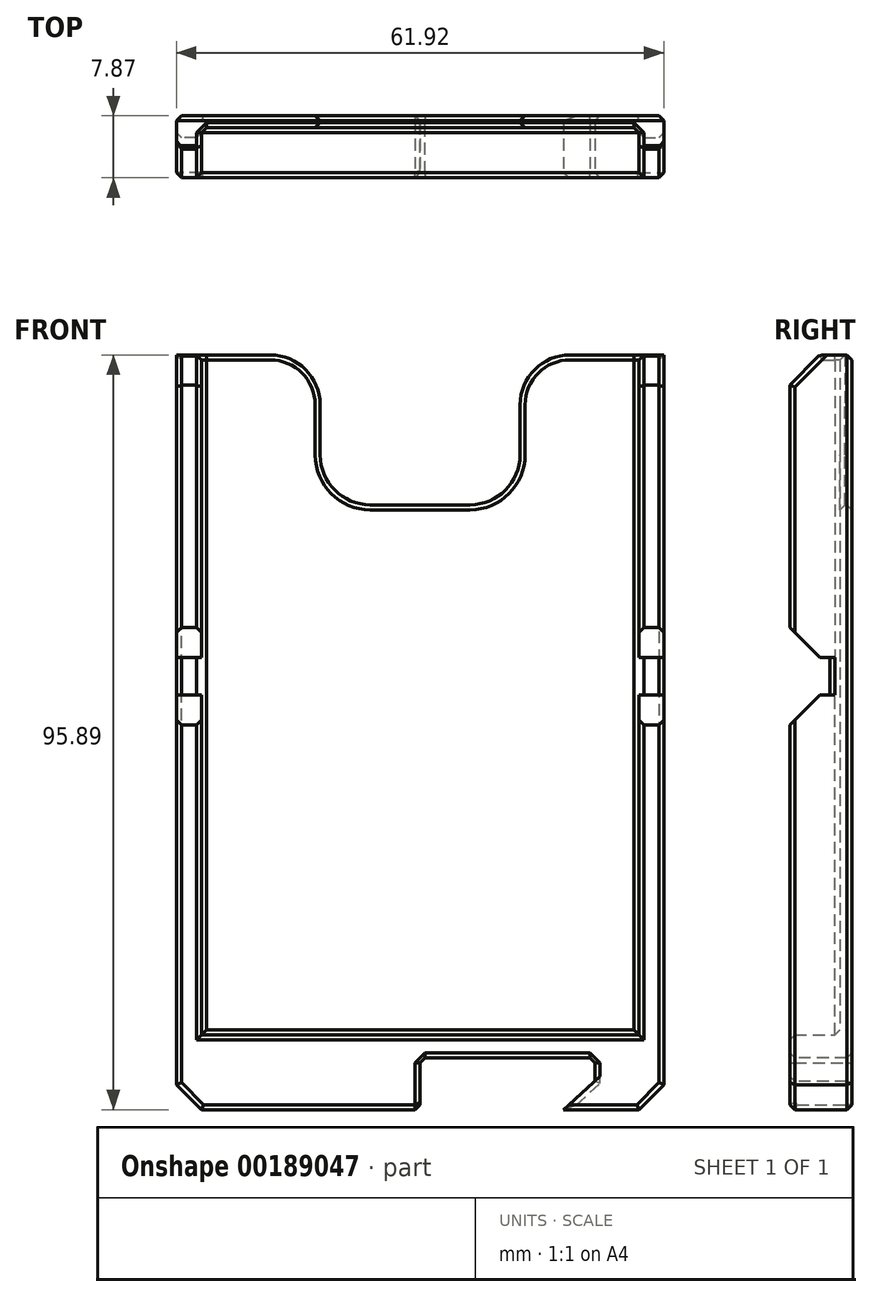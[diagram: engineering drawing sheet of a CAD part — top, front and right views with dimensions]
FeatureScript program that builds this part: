
annotation { "Feature Type Name" : "Feature", "Feature Type Description" : "" }
export const myFeature = defineFeature(function(context is Context, id is Id, definition is map)
    precondition{}
    {
        {
            var Q0;
            Q0=qCreatedBy(makeId("Front.planeOp"),FACE);
            var sketch = newSketch(context, id + "F0", { "sketchPlane" : qUnion([Q0])});
            skLineSegment(sketch, "E0.bottom", {"start": v(-19.05, 43.18) * mm, "end": v(-30.96, 43.18) * mm});
            skLineSegment(sketch, "E0.top", {"start": v(27.78, -43.18) * mm, "end": v(-27.78, -43.18) * mm});
            skLineSegment(sketch, "E0.left", {"start": v(27.78, 43.18) * mm, "end": v(27.78, -43.18) * mm});
            skLineSegment(sketch, "E0.right", {"start": v(-27.78, 43.18) * mm, "end": v(-27.78, -43.18) * mm});
            skPoint(sketch, "E0.middle", {"position": v(0, 0) * mm});
            skLineSegment(sketch, "E1.2", {"start": v(30.96, 43.18) * mm, "end": v(30.96, -52.7) * mm});
            skLineSegment(sketch, "E2.0", {"start": v(-30.96, 43.18) * mm, "end": v(-30.96, -52.7) * mm});
            skLineSegment(sketch, "E3.0", {"start": v(30.96, -52.7) * mm, "end": v(-30.96, -52.7) * mm});
            skLineSegment(sketch, "E4", {"start": v(27.78, 0) * mm, "end": v(30.96, 0) * mm});
            skLineSegment(sketch, "E5", {"start": v(-27.78, 0) * mm, "end": v(-30.96, 0) * mm});
            skLineSegment(sketch, "E6.0", {"start": v(-27.78, 4.76) * mm, "end": v(-30.96, 4.76) * mm});
            skLineSegment(sketch, "E7.0", {"start": v(27.78, 4.76) * mm, "end": v(30.96, 4.76) * mm});
            skLineSegment(sketch, "E8.bottom", {"start": v(6.35, 24.13) * mm, "end": v(-6.35, 24.13) * mm});
            skLineSegment(sketch, "E8.top", {"start": v(12.7, 62.23) * mm, "end": v(-12.7, 62.23) * mm});
            skLineSegment(sketch, "E8.left", {"start": v(12.7, 30.48) * mm, "end": v(12.7, 36.83) * mm});
            skLineSegment(sketch, "E8.right", {"start": v(-12.7, 30.48) * mm, "end": v(-12.7, 36.83) * mm});
            skPoint(sketch, "E8.middle", {"position": v(0, 43.18) * mm});
            skPoint(sketch, "E9.visualSharp", {"position": v(-12.7, 24.13) * mm});
            skArc(sketch, "E9.filletArc", {"start": v(-12.7, 30.48) * mm, "mid": v(-10.84, 25.99) * mm, "end": v(-6.35, 24.13) * mm});
            skPoint(sketch, "E10.visualSharp", {"position": v(12.7, 24.13) * mm});
            skArc(sketch, "E10.filletArc", {"start": v(6.35, 24.13) * mm, "mid": v(10.84, 25.99) * mm, "end": v(12.7, 30.48) * mm});
            skPoint(sketch, "E11.newPointA", {"position": v(-12.7, 62.23) * mm});
            skPoint(sketch, "E11.newPointB", {"position": v(30.96, 43.18) * mm});
            skArc(sketch, "E11.filletArc", {"start": v(-12.7, 36.83) * mm, "mid": v(-14.56, 41.32) * mm, "end": v(-19.05, 43.18) * mm});
            skLineSegment(sketch, "E12", {"start": v(27.78, 43.18) * mm, "end": v(19.05, 43.18) * mm});
            skArc(sketch, "E13.filletArc", {"start": v(19.05, 43.18) * mm, "mid": v(14.56, 41.32) * mm, "end": v(12.7, 36.83) * mm});
            skLineSegment(sketch, "E14", {"start": v(30.96, 43.18) * mm, "end": v(27.78, 43.18) * mm});
            skSolve(sketch);
        }
        {
            var Q0;
            {var subQ5=sQuery(id+"F0.wireOp",EDGE,"E0.top");Q0=makeQuery(id+"F0.imprint","IMPRINT",FACE,{"disambiguationData":[TD([[makeQuery(id+"F0.imprint","IMPRINT",EDGE,{"derivedFrom":subQ5}),-1.0]])]});}
            var Q1;
            {var subQ5=sQuery(id+"F0.wireOp",EDGE,"E6.0");Q1=makeQuery(id+"F0.imprint","IMPRINT",FACE,{"disambiguationData":[TD([[makeQuery(id+"F0.imprint","IMPRINT",EDGE,{"derivedFrom":subQ5}),-1.0]])]});}
            var Q2;
            {var subQ0=sQuery(id+"F0.wireOp",EDGE,"E5");Q2=makeQuery(id+"F0.imprint","IMPRINT",FACE,{"disambiguationData":[TD([[makeQuery(id+"F0.imprint","IMPRINT",EDGE,{"derivedFrom":subQ0}),-1.0]])]});}
            var Q3;
            {var subQ0=sQuery(id+"F0.wireOp",EDGE,"E4");Q3=makeQuery(id+"F0.imprint","IMPRINT",FACE,{"disambiguationData":[TD([[makeQuery(id+"F0.imprint","IMPRINT",EDGE,{"derivedFrom":subQ0}),1.0]])]});}
            var Q4;
            {var subQ5=sQuery(id+"F0.wireOp",EDGE,"E7.0");Q4=makeQuery(id+"F0.imprint","IMPRINT",FACE,{"disambiguationData":[TD([[makeQuery(id+"F0.imprint","IMPRINT",EDGE,{"derivedFrom":subQ5}),1.0]])]});}
            var Q5;
            {var subQ4=sQuery(id+"F0.wireOp",EDGE,"E0.top");Q5=makeQuery(id+"F0.imprint","IMPRINT",FACE,{"disambiguationData":[TD([[makeQuery(id+"F0.imprint","IMPRINT",EDGE,{"derivedFrom":subQ4}),1.0]])]});}
            extrude(context, id + "F1", {"entities" : qUnion([Q0, Q1, Q2, Q3, Q4, Q5]), "oppositeDirection" : true, "depth" : 1.52 * mm});
        }
        {
            var Q0;
            {var subQ4=sQuery(id+"F0.wireOp",EDGE,"E0.top");Q0=makeQuery(id+"F0.imprint","IMPRINT",FACE,{"disambiguationData":[TD([[makeQuery(id+"F0.imprint","IMPRINT",EDGE,{"derivedFrom":subQ4}),1.0]])]});}
            var Q1;
            {var subQ5=sQuery(id+"F0.wireOp",EDGE,"E7.0");Q1=makeQuery(id+"F0.imprint","IMPRINT",FACE,{"disambiguationData":[TD([[makeQuery(id+"F0.imprint","IMPRINT",EDGE,{"derivedFrom":subQ5}),1.0]])]});}
            var Q2;
            {var subQ5=sQuery(id+"F0.wireOp",EDGE,"E6.0");Q2=makeQuery(id+"F0.imprint","IMPRINT",FACE,{"disambiguationData":[TD([[makeQuery(id+"F0.imprint","IMPRINT",EDGE,{"derivedFrom":subQ5}),-1.0]])]});}
            extrude(context, id + "F2", {"entities" : qUnion([Q0, Q1, Q2]), "depth" : 6.35 * mm});
        }
        {
            var Q0;
            {var subQ0=sQuery(id+"F0.wireOp",EDGE,"E5");Q0=makeQuery(id+"F0.imprint","IMPRINT",FACE,{"disambiguationData":[TD([[makeQuery(id+"F0.imprint","IMPRINT",EDGE,{"derivedFrom":subQ0}),-1.0]])]});}
            var Q1;
            {var subQ0=sQuery(id+"F0.wireOp",EDGE,"E4");Q1=makeQuery(id+"F0.imprint","IMPRINT",FACE,{"disambiguationData":[TD([[makeQuery(id+"F0.imprint","IMPRINT",EDGE,{"derivedFrom":subQ0}),1.0]])]});}
            extrude(context, id + "F3", {"entities" : qUnion([Q0, Q1]), "depth" : 1.27 * mm});
        }
        {
            var Q0;
            Q0=makeQuery(id+"F2.opExtrude","SWEPT_BODY",BODY,{"disambiguationData":[OSD([sQuery(id+"F0.wireOp",EDGE,"E0.bottom"),sQuery(id+"F0.wireOp",EDGE,"E0.right"),sQuery(id+"F0.wireOp",EDGE,"E2.0"),sQuery(id+"F0.wireOp",EDGE,"E6.0")])]});
            var Q1;
            Q1=makeQuery(id+"F3.opExtrude","SWEPT_BODY",BODY,{"disambiguationData":[OSD([sQuery(id+"F0.wireOp",EDGE,"E0.right"),sQuery(id+"F0.wireOp",EDGE,"E2.0"),sQuery(id+"F0.wireOp",EDGE,"E5"),sQuery(id+"F0.wireOp",EDGE,"E6.0")])]});
            var Q2;
            Q2=makeQuery(id+"F2.opExtrude","SWEPT_BODY",BODY,{"disambiguationData":[OSD([sQuery(id+"F0.wireOp",EDGE,"E0.top"),sQuery(id+"F0.wireOp",EDGE,"E0.left"),sQuery(id+"F0.wireOp",EDGE,"E0.right"),sQuery(id+"F0.wireOp",EDGE,"E1.2"),sQuery(id+"F0.wireOp",EDGE,"E2.0"),sQuery(id+"F0.wireOp",EDGE,"E3.0"),sQuery(id+"F0.wireOp",EDGE,"E4"),sQuery(id+"F0.wireOp",EDGE,"E5")])]});
            var Q3;
            Q3=makeQuery(id+"F3.opExtrude","SWEPT_BODY",BODY,{"disambiguationData":[OSD([sQuery(id+"F0.wireOp",EDGE,"E0.left"),sQuery(id+"F0.wireOp",EDGE,"E1.2"),sQuery(id+"F0.wireOp",EDGE,"E4"),sQuery(id+"F0.wireOp",EDGE,"E7.0")])]});
            var Q4;
            Q4=makeQuery(id+"F2.opExtrude","SWEPT_BODY",BODY,{"disambiguationData":[OSD([sQuery(id+"F0.wireOp",EDGE,"E0.bottom"),sQuery(id+"F0.wireOp",EDGE,"E0.left"),sQuery(id+"F0.wireOp",EDGE,"E1.2"),sQuery(id+"F0.wireOp",EDGE,"E7.0")])]});
            booleanBodies(context, id + "F4", {"operationType" : BooleanOperationType.UNION, "tools" : qUnion([Q0, Q1, Q2, Q3, Q4])});
        }
        {
            var Q0;
            Q0=makeQuery(id+"F2.opExtrude","CAP_EDGE",EDGE,{"disambiguationData":[OSD([sQuery(id+"F0.wireOp",EDGE,"E6.0")])],"isStart":false});
            var Q1;
            Q1=makeQuery(id+"F2.opExtrude","CAP_EDGE",EDGE,{"disambiguationData":[OSD([sQuery(id+"F0.wireOp",EDGE,"E5")])],"isStart":false});
            var Q2;
            Q2=makeQuery(id+"F2.opExtrude","CAP_EDGE",EDGE,{"disambiguationData":[OSD([sQuery(id+"F0.wireOp",EDGE,"E7.0")])],"isStart":false});
            var Q3;
            Q3=makeQuery(id+"F2.opExtrude","CAP_EDGE",EDGE,{"disambiguationData":[OSD([sQuery(id+"F0.wireOp",EDGE,"E4")])],"isStart":false});
            var Q4;
            {var subQ0=sQuery(id+"F0.wireOp",EDGE,"E0.bottom");Q4=makeQuery(id+"F2.opExtrude","CAP_EDGE",EDGE,{"disambiguationData":[OSD([subQ0]),TDD([makeQuery(id+"F0.imprint","IMPRINT",EDGE,{"disambiguationData":[TD([[makeQuery(id+"F0.imprint","INTERSECT",VERTEX,{"derivedFrom":[subQ0,sQuery(id+"F0.wireOp",EDGE,"E2.0")]}),1.0]])],"derivedFrom":subQ0})])],"isStart":false});}
            var Q5;
            {var subQ0=sQuery(id+"F0.wireOp",EDGE,"E0.bottom");Q5=makeQuery(id+"F2.opExtrude","CAP_EDGE",EDGE,{"disambiguationData":[OSD([subQ0]),TDD([makeQuery(id+"F0.imprint","IMPRINT",EDGE,{"disambiguationData":[TD([[makeQuery(id+"F0.imprint","INTERSECT",VERTEX,{"derivedFrom":[subQ0,sQuery(id+"F0.wireOp",EDGE,"E1.2")]}),-1.0]])],"derivedFrom":subQ0})])],"isStart":false});}
            var Q6;
            Q6=makeQuery(id+"F2.opExtrude","CAP_EDGE",EDGE,{"disambiguationData":[OSD([sQuery(id+"F0.wireOp",EDGE,"E14")])],"isStart":false});
            chamfer(context, id + "F5", {"entities" : qUnion([Q0, Q1, Q2, Q3, Q4, Q5, Q6]), "width" : 3.8 * mm, "tangentPropagation" : true});
        }
        {
            var Q0;
            {var subQ0=sQuery(id+"F0.wireOp",EDGE,"E0.left");Q0=makeQuery(id+"F2.opExtrude","CAP_EDGE",EDGE,{"disambiguationData":[OSD([subQ0]),TDD([makeQuery(id+"F0.imprint","IMPRINT",EDGE,{"disambiguationData":[TD([[makeQuery(id+"F0.imprint","INTERSECT",VERTEX,{"derivedFrom":[sQuery(id+"F0.wireOp",EDGE,"E0.top"),subQ0]}),1.0]])],"derivedFrom":subQ0})])],"isStart":false});}
            var Q1;
            Q1=makeQuery(id+"F2.opExtrude","CAP_EDGE",EDGE,{"disambiguationData":[OSD([sQuery(id+"F0.wireOp",EDGE,"E0.top")])],"isStart":false});
            var Q2;
            {var subQ0=sQuery(id+"F0.wireOp",EDGE,"E0.right");Q2=makeQuery(id+"F2.opExtrude","CAP_EDGE",EDGE,{"disambiguationData":[OSD([subQ0]),TDD([makeQuery(id+"F0.imprint","IMPRINT",EDGE,{"disambiguationData":[TD([[makeQuery(id+"F0.imprint","INTERSECT",VERTEX,{"derivedFrom":[sQuery(id+"F0.wireOp",EDGE,"E0.top"),subQ0]}),1.0]])],"derivedFrom":subQ0})])],"isStart":false});}
            var Q3;
            {var subQ0=sQuery(id+"F0.wireOp",EDGE,"E0.right");Q3=makeQuery(id+"F2.opExtrude","CAP_EDGE",EDGE,{"disambiguationData":[OSD([subQ0]),TDD([makeQuery(id+"F0.imprint","IMPRINT",EDGE,{"disambiguationData":[TD([[makeQuery(id+"F0.imprint","INTERSECT",VERTEX,{"derivedFrom":[sQuery(id+"F0.wireOp",EDGE,"E0.bottom"),subQ0]}),-1.0]])],"derivedFrom":subQ0})])],"isStart":false});}
            var Q4;
            Q4=makeQuery(id+"F3.opExtrude","CAP_EDGE",EDGE,{"disambiguationData":[OSD([sQuery(id+"F0.wireOp",EDGE,"E2.0")])],"isStart":false});
            var Q5;
            Q5=makeQuery(id+"F3.opExtrude","CAP_EDGE",EDGE,{"disambiguationData":[OSD([sQuery(id+"F0.wireOp",EDGE,"E0.right")])],"isStart":false});
            var Q6;
            Q6=makeQuery(id+"F3.opExtrude","CAP_EDGE",EDGE,{"disambiguationData":[OSD([sQuery(id+"F0.wireOp",EDGE,"E0.left")])],"isStart":false});
            var Q7;
            Q7=makeQuery(id+"F3.opExtrude","CAP_EDGE",EDGE,{"disambiguationData":[OSD([sQuery(id+"F0.wireOp",EDGE,"E1.2")])],"isStart":false});
            var Q8;
            {var subQ0=sQuery(id+"F0.wireOp",EDGE,"E1.2");Q8=makeQuery(id+"F2.opExtrude","CAP_EDGE",EDGE,{"disambiguationData":[OSD([subQ0]),TDD([makeQuery(id+"F0.imprint","IMPRINT",EDGE,{"disambiguationData":[TD([[makeQuery(id+"F0.imprint","INTERSECT",VERTEX,{"derivedFrom":[subQ0,sQuery(id+"F0.wireOp",EDGE,"E14")]}),-1.0]])],"derivedFrom":subQ0})])],"isStart":false});}
            var Q9;
            {var subQ0=sQuery(id+"F0.wireOp",EDGE,"E1.2");Q9=makeQuery(id+"F2.opExtrude","CAP_EDGE",EDGE,{"disambiguationData":[OSD([subQ0]),TDD([makeQuery(id+"F0.imprint","IMPRINT",EDGE,{"disambiguationData":[TD([[makeQuery(id+"F0.imprint","INTERSECT",VERTEX,{"derivedFrom":[subQ0,sQuery(id+"F0.wireOp",EDGE,"E3.0")]}),1.0]])],"derivedFrom":subQ0})])],"isStart":false});}
            var Q10;
            {var subQ0=sQuery(id+"F0.wireOp",EDGE,"E2.0");Q10=makeQuery(id+"F2.opExtrude","CAP_EDGE",EDGE,{"disambiguationData":[OSD([subQ0]),TDD([makeQuery(id+"F0.imprint","IMPRINT",EDGE,{"disambiguationData":[TD([[makeQuery(id+"F0.imprint","INTERSECT",VERTEX,{"derivedFrom":[subQ0,sQuery(id+"F0.wireOp",EDGE,"E3.0")]}),1.0]])],"derivedFrom":subQ0})])],"isStart":false});}
            var Q11;
            {var subQ0=sQuery(id+"F0.wireOp",EDGE,"E2.0");Q11=makeQuery(id+"F2.opExtrude","CAP_EDGE",EDGE,{"disambiguationData":[OSD([subQ0]),TDD([makeQuery(id+"F0.imprint","IMPRINT",EDGE,{"disambiguationData":[TD([[makeQuery(id+"F0.imprint","INTERSECT",VERTEX,{"derivedFrom":[sQuery(id+"F0.wireOp",EDGE,"E0.bottom"),subQ0]}),-1.0]])],"derivedFrom":subQ0})])],"isStart":false});}
            var Q12;
            {var subQ0=sQuery(id+"F0.wireOp",EDGE,"E0.left");Q12=makeQuery(id+"F2.opExtrude","CAP_EDGE",EDGE,{"disambiguationData":[OSD([subQ0]),TDD([makeQuery(id+"F0.imprint","IMPRINT",EDGE,{"disambiguationData":[TD([[makeQuery(id+"F0.imprint","INTERSECT",VERTEX,{"derivedFrom":[subQ0,sQuery(id+"F0.wireOp",EDGE,"E7.0")]}),1.0]])],"derivedFrom":subQ0})])],"isStart":false});}
            var Q13;
            {var subQ0=sQuery(id+"F0.wireOp",EDGE,"E0.left");var subQ1=sQuery(id+"F0.wireOp",EDGE,"E14");Q13=makeQuery(id+"F5.opChamfer","BLEND_EDGE",EDGE,{"blendedFrom":[makeQuery(id+"F2.opExtrude","CAP_EDGE",EDGE,{"disambiguationData":[OSD([subQ1])],"isStart":false}),makeQuery(id+"F4.opBoolean","MERGE",FACE,{"derivedFrom":[makeQuery(id+"F2.opExtrude","SWEPT_FACE",FACE,{"disambiguationData":[OSD([subQ0]),TDD([makeQuery(id+"F0.imprint","IMPRINT",EDGE,{"disambiguationData":[TD([[makeQuery(id+"F0.imprint","INTERSECT",VERTEX,{"derivedFrom":[subQ0,sQuery(id+"F0.wireOp",EDGE,"E7.0")]}),1.0]])],"derivedFrom":subQ0})])]}),makeQuery(id+"F2.opExtrude","SWEPT_FACE",FACE,{"disambiguationData":[OSD([subQ0]),TDD([makeQuery(id+"F0.imprint","IMPRINT",EDGE,{"disambiguationData":[TD([[makeQuery(id+"F0.imprint","INTERSECT",VERTEX,{"derivedFrom":[sQuery(id+"F0.wireOp",EDGE,"E0.top"),subQ0]}),1.0]])],"derivedFrom":subQ0})])]}),makeQuery(id+"F3.opExtrude","SWEPT_FACE",FACE,{"disambiguationData":[OSD([subQ0])]})]})],"blendedInto":[makeQuery(id+"F4.opBoolean","MERGE",FACE,{"derivedFrom":[makeQuery(id+"F2.opExtrude","SWEPT_FACE",FACE,{"disambiguationData":[OSD([subQ0]),TDD([makeQuery(id+"F0.imprint","IMPRINT",EDGE,{"disambiguationData":[TD([[makeQuery(id+"F0.imprint","INTERSECT",VERTEX,{"derivedFrom":[subQ0,sQuery(id+"F0.wireOp",EDGE,"E7.0")]}),1.0]])],"derivedFrom":subQ0})])]}),makeQuery(id+"F2.opExtrude","SWEPT_FACE",FACE,{"disambiguationData":[OSD([subQ0]),TDD([makeQuery(id+"F0.imprint","IMPRINT",EDGE,{"disambiguationData":[TD([[makeQuery(id+"F0.imprint","INTERSECT",VERTEX,{"derivedFrom":[sQuery(id+"F0.wireOp",EDGE,"E0.top"),subQ0]}),1.0]])],"derivedFrom":subQ0})])]}),makeQuery(id+"F3.opExtrude","SWEPT_FACE",FACE,{"disambiguationData":[OSD([subQ0])]})]})]});}
            var Q14;
            {var subQ0=sQuery(id+"F0.wireOp",EDGE,"E1.2");var subQ1=sQuery(id+"F0.wireOp",EDGE,"E14");Q14=makeQuery(id+"F5.opChamfer","BLEND_EDGE",EDGE,{"blendedFrom":[makeQuery(id+"F2.opExtrude","CAP_EDGE",EDGE,{"disambiguationData":[OSD([subQ1])],"isStart":false}),makeQuery(id+"F4.opBoolean","MERGE",FACE,{"derivedFrom":[makeQuery(id+"F2.opExtrude","SWEPT_FACE",FACE,{"disambiguationData":[OSD([subQ0]),TDD([makeQuery(id+"F0.imprint","IMPRINT",EDGE,{"disambiguationData":[TD([[makeQuery(id+"F0.imprint","INTERSECT",VERTEX,{"derivedFrom":[subQ0,subQ1]}),-1.0]])],"derivedFrom":subQ0})])]}),makeQuery(id+"F2.opExtrude","SWEPT_FACE",FACE,{"disambiguationData":[OSD([subQ0]),TDD([makeQuery(id+"F0.imprint","IMPRINT",EDGE,{"disambiguationData":[TD([[makeQuery(id+"F0.imprint","INTERSECT",VERTEX,{"derivedFrom":[subQ0,sQuery(id+"F0.wireOp",EDGE,"E3.0")]}),1.0]])],"derivedFrom":subQ0})])]}),makeQuery(id+"F3.opExtrude","SWEPT_FACE",FACE,{"disambiguationData":[OSD([subQ0])]})]})],"blendedInto":[makeQuery(id+"F4.opBoolean","MERGE",FACE,{"derivedFrom":[makeQuery(id+"F2.opExtrude","SWEPT_FACE",FACE,{"disambiguationData":[OSD([subQ0]),TDD([makeQuery(id+"F0.imprint","IMPRINT",EDGE,{"disambiguationData":[TD([[makeQuery(id+"F0.imprint","INTERSECT",VERTEX,{"derivedFrom":[subQ0,subQ1]}),-1.0]])],"derivedFrom":subQ0})])]}),makeQuery(id+"F2.opExtrude","SWEPT_FACE",FACE,{"disambiguationData":[OSD([subQ0]),TDD([makeQuery(id+"F0.imprint","IMPRINT",EDGE,{"disambiguationData":[TD([[makeQuery(id+"F0.imprint","INTERSECT",VERTEX,{"derivedFrom":[subQ0,sQuery(id+"F0.wireOp",EDGE,"E3.0")]}),1.0]])],"derivedFrom":subQ0})])]}),makeQuery(id+"F3.opExtrude","SWEPT_FACE",FACE,{"disambiguationData":[OSD([subQ0])]})]})]});}
            var Q15;
            {var subQ0=sQuery(id+"F0.wireOp",EDGE,"E2.0");var subQ1=sQuery(id+"F0.wireOp",EDGE,"E0.bottom");Q15=makeQuery(id+"F5.opChamfer","BLEND_EDGE",EDGE,{"blendedFrom":[makeQuery(id+"F2.opExtrude","CAP_EDGE",EDGE,{"disambiguationData":[OSD([subQ1])],"isStart":false}),makeQuery(id+"F4.opBoolean","MERGE",FACE,{"derivedFrom":[makeQuery(id+"F2.opExtrude","SWEPT_FACE",FACE,{"disambiguationData":[OSD([subQ0]),TDD([makeQuery(id+"F0.imprint","IMPRINT",EDGE,{"disambiguationData":[TD([[makeQuery(id+"F0.imprint","INTERSECT",VERTEX,{"derivedFrom":[subQ1,subQ0]}),-1.0]])],"derivedFrom":subQ0})])]}),makeQuery(id+"F2.opExtrude","SWEPT_FACE",FACE,{"disambiguationData":[OSD([subQ0]),TDD([makeQuery(id+"F0.imprint","IMPRINT",EDGE,{"disambiguationData":[TD([[makeQuery(id+"F0.imprint","INTERSECT",VERTEX,{"derivedFrom":[subQ0,sQuery(id+"F0.wireOp",EDGE,"E3.0")]}),1.0]])],"derivedFrom":subQ0})])]}),makeQuery(id+"F3.opExtrude","SWEPT_FACE",FACE,{"disambiguationData":[OSD([subQ0])]})]})],"blendedInto":[makeQuery(id+"F4.opBoolean","MERGE",FACE,{"derivedFrom":[makeQuery(id+"F2.opExtrude","SWEPT_FACE",FACE,{"disambiguationData":[OSD([subQ0]),TDD([makeQuery(id+"F0.imprint","IMPRINT",EDGE,{"disambiguationData":[TD([[makeQuery(id+"F0.imprint","INTERSECT",VERTEX,{"derivedFrom":[subQ1,subQ0]}),-1.0]])],"derivedFrom":subQ0})])]}),makeQuery(id+"F2.opExtrude","SWEPT_FACE",FACE,{"disambiguationData":[OSD([subQ0]),TDD([makeQuery(id+"F0.imprint","IMPRINT",EDGE,{"disambiguationData":[TD([[makeQuery(id+"F0.imprint","INTERSECT",VERTEX,{"derivedFrom":[subQ0,sQuery(id+"F0.wireOp",EDGE,"E3.0")]}),1.0]])],"derivedFrom":subQ0})])]}),makeQuery(id+"F3.opExtrude","SWEPT_FACE",FACE,{"disambiguationData":[OSD([subQ0])]})]})]});}
            var Q16;
            {var subQ0=sQuery(id+"F0.wireOp",EDGE,"E0.right");var subQ1=sQuery(id+"F0.wireOp",EDGE,"E0.bottom");Q16=makeQuery(id+"F5.opChamfer","BLEND_EDGE",EDGE,{"blendedFrom":[makeQuery(id+"F2.opExtrude","CAP_EDGE",EDGE,{"disambiguationData":[OSD([subQ1])],"isStart":false}),makeQuery(id+"F4.opBoolean","MERGE",FACE,{"derivedFrom":[makeQuery(id+"F2.opExtrude","SWEPT_FACE",FACE,{"disambiguationData":[OSD([subQ0]),TDD([makeQuery(id+"F0.imprint","IMPRINT",EDGE,{"disambiguationData":[TD([[makeQuery(id+"F0.imprint","INTERSECT",VERTEX,{"derivedFrom":[subQ1,subQ0]}),-1.0]])],"derivedFrom":subQ0})])]}),makeQuery(id+"F2.opExtrude","SWEPT_FACE",FACE,{"disambiguationData":[OSD([subQ0]),TDD([makeQuery(id+"F0.imprint","IMPRINT",EDGE,{"disambiguationData":[TD([[makeQuery(id+"F0.imprint","INTERSECT",VERTEX,{"derivedFrom":[sQuery(id+"F0.wireOp",EDGE,"E0.top"),subQ0]}),1.0]])],"derivedFrom":subQ0})])]}),makeQuery(id+"F3.opExtrude","SWEPT_FACE",FACE,{"disambiguationData":[OSD([subQ0])]})]})],"blendedInto":[makeQuery(id+"F4.opBoolean","MERGE",FACE,{"derivedFrom":[makeQuery(id+"F2.opExtrude","SWEPT_FACE",FACE,{"disambiguationData":[OSD([subQ0]),TDD([makeQuery(id+"F0.imprint","IMPRINT",EDGE,{"disambiguationData":[TD([[makeQuery(id+"F0.imprint","INTERSECT",VERTEX,{"derivedFrom":[subQ1,subQ0]}),-1.0]])],"derivedFrom":subQ0})])]}),makeQuery(id+"F2.opExtrude","SWEPT_FACE",FACE,{"disambiguationData":[OSD([subQ0]),TDD([makeQuery(id+"F0.imprint","IMPRINT",EDGE,{"disambiguationData":[TD([[makeQuery(id+"F0.imprint","INTERSECT",VERTEX,{"derivedFrom":[sQuery(id+"F0.wireOp",EDGE,"E0.top"),subQ0]}),1.0]])],"derivedFrom":subQ0})])]}),makeQuery(id+"F3.opExtrude","SWEPT_FACE",FACE,{"disambiguationData":[OSD([subQ0])]})]})]});}
            var Q17;
            {var subQ0=sQuery(id+"F0.wireOp",EDGE,"E0.bottom");Q17=makeQuery(id+"F5.opChamfer","BLEND_EDGE",EDGE,{"blendedFrom":[makeQuery(id+"F2.opExtrude","CAP_EDGE",EDGE,{"disambiguationData":[OSD([subQ0])],"isStart":false}),makeQuery(id+"F2.opExtrude","SWEPT_FACE",FACE,{"disambiguationData":[OSD([subQ0])]})],"blendedInto":[makeQuery(id+"F2.opExtrude","SWEPT_FACE",FACE,{"disambiguationData":[OSD([subQ0])]})]});}
            var Q18;
            {var subQ0=sQuery(id+"F0.wireOp",EDGE,"E14");Q18=makeQuery(id+"F5.opChamfer","BLEND_EDGE",EDGE,{"blendedFrom":[makeQuery(id+"F2.opExtrude","CAP_EDGE",EDGE,{"disambiguationData":[OSD([subQ0])],"isStart":false}),makeQuery(id+"F2.opExtrude","SWEPT_FACE",FACE,{"disambiguationData":[OSD([subQ0])]})],"blendedInto":[makeQuery(id+"F2.opExtrude","SWEPT_FACE",FACE,{"disambiguationData":[OSD([subQ0])]})]});}
            var Q19;
            Q19=makeQuery(id+"F2.opExtrude","CAP_EDGE",EDGE,{"disambiguationData":[OSD([sQuery(id+"F0.wireOp",EDGE,"E3.0")])],"isStart":false});
            chamfer(context, id + "F6", {"entities" : qUnion([Q0, Q1, Q2, Q3, Q4, Q5, Q6, Q7, Q8, Q9, Q10, Q11, Q12, Q13, Q14, Q15, Q16, Q17, Q18, Q19]), "width" : 0.64 * mm, "tangentPropagation" : true});
        }
        {
            var Q0;
            Q0=makeQuery(id+"F2.opExtrude","CAP_FACE",FACE,{"disambiguationData":[OSD([sQuery(id+"F0.wireOp",EDGE,"E0.top"),sQuery(id+"F0.wireOp",EDGE,"E0.left"),sQuery(id+"F0.wireOp",EDGE,"E0.right"),sQuery(id+"F0.wireOp",EDGE,"E1.2"),sQuery(id+"F0.wireOp",EDGE,"E2.0"),sQuery(id+"F0.wireOp",EDGE,"E3.0"),sQuery(id+"F0.wireOp",EDGE,"E4"),sQuery(id+"F0.wireOp",EDGE,"E5")])],"isStart":false});
            var sketch = newSketch(context, id + "F7", { "sketchPlane" : qUnion([Q0])});
            skLineSegment(sketch, "E15.bottom", {"start": v(0, -52.07) * mm, "end": v(22.23, -52.07) * mm});
            skLineSegment(sketch, "E15.top", {"start": v(0, -46.1) * mm, "end": v(22.23, -46.1) * mm});
            skLineSegment(sketch, "E15.left", {"start": v(0, -52.7) * mm, "end": v(0, -46.1) * mm});
            skLineSegment(sketch, "E15.right", {"start": v(22.23, -52.07) * mm, "end": v(22.23, -46.1) * mm});
            skLineSegment(sketch, "E16", {"start": v(22.23, -49.09) * mm, "end": v(18.22, -52.7) * mm});
            skLineSegment(sketch, "E17.0", {"start": v(30.96, -52.7) * mm, "end": v(-30.96, -52.7) * mm});
            skLineSegment(sketch, "E18", {"start": v(22.23, -52.07) * mm, "end": v(22.23, -52.7) * mm});
            skPoint(sketch, "E19.orphan", {"position": v(18.92, -52.07) * mm});
            skSolve(sketch);
        }
        {
            var Q0;
            Q0=makeQuery(id+"F1.opExtrude","SWEPT_BODY",BODY,{"disambiguationData":[OSD([sQuery(id+"F0.wireOp",EDGE,"E0.bottom"),sQuery(id+"F0.wireOp",EDGE,"E1.2"),sQuery(id+"F0.wireOp",EDGE,"E2.0"),sQuery(id+"F0.wireOp",EDGE,"E3.0"),sQuery(id+"F0.wireOp",EDGE,"E8.bottom"),sQuery(id+"F0.wireOp",EDGE,"E8.left"),sQuery(id+"F0.wireOp",EDGE,"E8.right"),sQuery(id+"F0.wireOp",EDGE,"E9.filletArc"),sQuery(id+"F0.wireOp",EDGE,"E10.filletArc"),sQuery(id+"F0.wireOp",EDGE,"E11.filletArc"),sQuery(id+"F0.wireOp",EDGE,"E12"),sQuery(id+"F0.wireOp",EDGE,"E13.filletArc"),sQuery(id+"F0.wireOp",EDGE,"E14")])]});
            var Q1;
            Q1=makeQuery(id+"F2.opExtrude","SWEPT_BODY",BODY,{"disambiguationData":[OSD([sQuery(id+"F0.wireOp",EDGE,"E0.bottom"),sQuery(id+"F0.wireOp",EDGE,"E0.right"),sQuery(id+"F0.wireOp",EDGE,"E2.0"),sQuery(id+"F0.wireOp",EDGE,"E6.0")])]});
            booleanBodies(context, id + "F8", {"operationType" : BooleanOperationType.UNION, "tools" : qUnion([Q0, Q1])});
        }
        {
            var Q0;
            {var subQ2=sQuery(id+"F7.wireOp",EDGE,"E15.top");Q0=makeQuery(id+"F7.imprint","IMPRINT",FACE,{"disambiguationData":[TD([[makeQuery(id+"F7.imprint","IMPRINT",EDGE,{"derivedFrom":subQ2}),-1.0]])]});}
            var Q1;
            {var subQ4=sQuery(id+"F7.wireOp",EDGE,"E16");var subQ6=sQuery(id+"F7.wireOp",EDGE,"E17.0");var subQ7=makeQuery(id+"F7.imprint","INTERSECT",VERTEX,{"derivedFrom":[subQ4,subQ6]});Q1=makeQuery(id+"F7.imprint","IMPRINT",FACE,{"disambiguationData":[TD([[makeQuery(id+"F7.imprint","IMPRINT",EDGE,{"disambiguationData":[TD([[subQ7,1.0]])],"derivedFrom":subQ4}),-1.0]])]});}
            extrude(context, id + "F9", {"entities" : qUnion([Q0, Q1]), "operationType" : NewBodyOperationType.REMOVE, "oppositeDirection" : true, "depth" : 25.4 * mm});
        }
        {
            var Q0;
            {var subQ0=sQuery(id+"F0.wireOp",EDGE,"E3.0");var subQ1=sQuery(id+"F0.wireOp",EDGE,"E1.2");Q0=makeQuery(id+"F8.opBoolean","MERGE",EDGE,{"derivedFrom":[makeQuery(id+"F1.opExtrude","SWEPT_EDGE",EDGE,{"disambiguationData":[OSD([subQ1,subQ0])]}),makeQuery(id+"F2.opExtrude","SWEPT_EDGE",EDGE,{"disambiguationData":[OSD([subQ1,subQ0])]})]});}
            var Q1;
            {var subQ0=sQuery(id+"F0.wireOp",EDGE,"E3.0");var subQ1=sQuery(id+"F0.wireOp",EDGE,"E2.0");Q1=makeQuery(id+"F8.opBoolean","MERGE",EDGE,{"derivedFrom":[makeQuery(id+"F1.opExtrude","SWEPT_EDGE",EDGE,{"disambiguationData":[OSD([subQ1,subQ0])]}),makeQuery(id+"F2.opExtrude","SWEPT_EDGE",EDGE,{"disambiguationData":[OSD([subQ1,subQ0])]})]});}
            chamfer(context, id + "F10", {"entities" : qUnion([Q0, Q1]), "width" : 3.17 * mm, "tangentPropagation" : true});
        }
        {
            var Q0;
            {var subQ0=sQuery(id+"F0.wireOp",EDGE,"E3.0");var subQ1=sQuery(id+"F0.wireOp",EDGE,"E1.2");Q0=makeQuery(id+"F10.opChamfer","BLEND_EDGE",EDGE,{"blendedFrom":[makeQuery(id+"F8.opBoolean","MERGE",EDGE,{"derivedFrom":[makeQuery(id+"F1.opExtrude","SWEPT_EDGE",EDGE,{"disambiguationData":[OSD([subQ1,subQ0])]}),makeQuery(id+"F2.opExtrude","SWEPT_EDGE",EDGE,{"disambiguationData":[OSD([subQ1,subQ0])]})]}),makeQuery(id+"F2.opExtrude","CAP_FACE",FACE,{"disambiguationData":[OSD([sQuery(id+"F0.wireOp",EDGE,"E0.top"),sQuery(id+"F0.wireOp",EDGE,"E0.left"),sQuery(id+"F0.wireOp",EDGE,"E0.right"),subQ1,sQuery(id+"F0.wireOp",EDGE,"E2.0"),subQ0,sQuery(id+"F0.wireOp",EDGE,"E4"),sQuery(id+"F0.wireOp",EDGE,"E5")])],"isStart":false})],"blendedInto":[makeQuery(id+"F2.opExtrude","CAP_FACE",FACE,{"disambiguationData":[OSD([sQuery(id+"F0.wireOp",EDGE,"E0.top"),sQuery(id+"F0.wireOp",EDGE,"E0.left"),sQuery(id+"F0.wireOp",EDGE,"E0.right"),subQ1,sQuery(id+"F0.wireOp",EDGE,"E2.0"),subQ0,sQuery(id+"F0.wireOp",EDGE,"E4"),sQuery(id+"F0.wireOp",EDGE,"E5")])],"isStart":false})]});}
            var Q1;
            {var subQ0=sQuery(id+"F0.wireOp",EDGE,"E3.0");var subQ1=sQuery(id+"F0.wireOp",EDGE,"E1.2");Q1=makeQuery(id+"F10.opChamfer","BLEND_EDGE",EDGE,{"blendedFrom":[makeQuery(id+"F8.opBoolean","MERGE",EDGE,{"derivedFrom":[makeQuery(id+"F1.opExtrude","SWEPT_EDGE",EDGE,{"disambiguationData":[OSD([subQ1,subQ0])]}),makeQuery(id+"F2.opExtrude","SWEPT_EDGE",EDGE,{"disambiguationData":[OSD([subQ1,subQ0])]})]}),makeQuery(id+"F1.opExtrude","CAP_FACE",FACE,{"disambiguationData":[OSD([sQuery(id+"F0.wireOp",EDGE,"E0.bottom"),subQ1,sQuery(id+"F0.wireOp",EDGE,"E2.0"),subQ0,sQuery(id+"F0.wireOp",EDGE,"E8.bottom"),sQuery(id+"F0.wireOp",EDGE,"E8.left"),sQuery(id+"F0.wireOp",EDGE,"E8.right"),sQuery(id+"F0.wireOp",EDGE,"E9.filletArc"),sQuery(id+"F0.wireOp",EDGE,"E10.filletArc"),sQuery(id+"F0.wireOp",EDGE,"E11.filletArc"),sQuery(id+"F0.wireOp",EDGE,"E12"),sQuery(id+"F0.wireOp",EDGE,"E13.filletArc"),sQuery(id+"F0.wireOp",EDGE,"E14")])],"isStart":false})],"blendedInto":[makeQuery(id+"F1.opExtrude","CAP_FACE",FACE,{"disambiguationData":[OSD([sQuery(id+"F0.wireOp",EDGE,"E0.bottom"),subQ1,sQuery(id+"F0.wireOp",EDGE,"E2.0"),subQ0,sQuery(id+"F0.wireOp",EDGE,"E8.bottom"),sQuery(id+"F0.wireOp",EDGE,"E8.left"),sQuery(id+"F0.wireOp",EDGE,"E8.right"),sQuery(id+"F0.wireOp",EDGE,"E9.filletArc"),sQuery(id+"F0.wireOp",EDGE,"E10.filletArc"),sQuery(id+"F0.wireOp",EDGE,"E11.filletArc"),sQuery(id+"F0.wireOp",EDGE,"E12"),sQuery(id+"F0.wireOp",EDGE,"E13.filletArc"),sQuery(id+"F0.wireOp",EDGE,"E14")])],"isStart":false})]});}
            var Q2;
            {var subQ0=sQuery(id+"F0.wireOp",EDGE,"E3.0");var subQ1=sQuery(id+"F0.wireOp",EDGE,"E2.0");Q2=makeQuery(id+"F10.opChamfer","BLEND_EDGE",EDGE,{"blendedFrom":[makeQuery(id+"F8.opBoolean","MERGE",EDGE,{"derivedFrom":[makeQuery(id+"F1.opExtrude","SWEPT_EDGE",EDGE,{"disambiguationData":[OSD([subQ1,subQ0])]}),makeQuery(id+"F2.opExtrude","SWEPT_EDGE",EDGE,{"disambiguationData":[OSD([subQ1,subQ0])]})]}),makeQuery(id+"F2.opExtrude","CAP_FACE",FACE,{"disambiguationData":[OSD([sQuery(id+"F0.wireOp",EDGE,"E0.top"),sQuery(id+"F0.wireOp",EDGE,"E0.left"),sQuery(id+"F0.wireOp",EDGE,"E0.right"),sQuery(id+"F0.wireOp",EDGE,"E1.2"),subQ1,subQ0,sQuery(id+"F0.wireOp",EDGE,"E4"),sQuery(id+"F0.wireOp",EDGE,"E5")])],"isStart":false})],"blendedInto":[makeQuery(id+"F2.opExtrude","CAP_FACE",FACE,{"disambiguationData":[OSD([sQuery(id+"F0.wireOp",EDGE,"E0.top"),sQuery(id+"F0.wireOp",EDGE,"E0.left"),sQuery(id+"F0.wireOp",EDGE,"E0.right"),sQuery(id+"F0.wireOp",EDGE,"E1.2"),subQ1,subQ0,sQuery(id+"F0.wireOp",EDGE,"E4"),sQuery(id+"F0.wireOp",EDGE,"E5")])],"isStart":false})]});}
            var Q3;
            {var subQ0=sQuery(id+"F0.wireOp",EDGE,"E3.0");var subQ1=sQuery(id+"F0.wireOp",EDGE,"E2.0");Q3=makeQuery(id+"F10.opChamfer","BLEND_EDGE",EDGE,{"blendedFrom":[makeQuery(id+"F8.opBoolean","MERGE",EDGE,{"derivedFrom":[makeQuery(id+"F1.opExtrude","SWEPT_EDGE",EDGE,{"disambiguationData":[OSD([subQ1,subQ0])]}),makeQuery(id+"F2.opExtrude","SWEPT_EDGE",EDGE,{"disambiguationData":[OSD([subQ1,subQ0])]})]}),makeQuery(id+"F1.opExtrude","CAP_FACE",FACE,{"disambiguationData":[OSD([sQuery(id+"F0.wireOp",EDGE,"E0.bottom"),sQuery(id+"F0.wireOp",EDGE,"E1.2"),subQ1,subQ0,sQuery(id+"F0.wireOp",EDGE,"E8.bottom"),sQuery(id+"F0.wireOp",EDGE,"E8.left"),sQuery(id+"F0.wireOp",EDGE,"E8.right"),sQuery(id+"F0.wireOp",EDGE,"E9.filletArc"),sQuery(id+"F0.wireOp",EDGE,"E10.filletArc"),sQuery(id+"F0.wireOp",EDGE,"E11.filletArc"),sQuery(id+"F0.wireOp",EDGE,"E12"),sQuery(id+"F0.wireOp",EDGE,"E13.filletArc"),sQuery(id+"F0.wireOp",EDGE,"E14")])],"isStart":false})],"blendedInto":[makeQuery(id+"F1.opExtrude","CAP_FACE",FACE,{"disambiguationData":[OSD([sQuery(id+"F0.wireOp",EDGE,"E0.bottom"),sQuery(id+"F0.wireOp",EDGE,"E1.2"),subQ1,subQ0,sQuery(id+"F0.wireOp",EDGE,"E8.bottom"),sQuery(id+"F0.wireOp",EDGE,"E8.left"),sQuery(id+"F0.wireOp",EDGE,"E8.right"),sQuery(id+"F0.wireOp",EDGE,"E9.filletArc"),sQuery(id+"F0.wireOp",EDGE,"E10.filletArc"),sQuery(id+"F0.wireOp",EDGE,"E11.filletArc"),sQuery(id+"F0.wireOp",EDGE,"E12"),sQuery(id+"F0.wireOp",EDGE,"E13.filletArc"),sQuery(id+"F0.wireOp",EDGE,"E14")])],"isStart":false})]});}
            var Q4;
            {var subQ1=sQuery(id+"F0.wireOp",EDGE,"E1.2");var subQ2=sQuery(id+"F0.wireOp",EDGE,"E3.0");Q4=makeQuery(id+"F9.boolean.opBoolean","SPLIT",EDGE,{"disambiguationData":[TD([makeQuery(id+"F1.opExtrude","SWEPT_FACE",FACE,{"disambiguationData":[OSD([subQ1])]})])],"derivedFrom":makeQuery(id+"F1.opExtrude","CAP_EDGE",EDGE,{"disambiguationData":[OSD([subQ2])],"isStart":false})});}
            var Q5;
            {var subQ0=sQuery(id+"F0.wireOp",EDGE,"E2.0");var subQ2=sQuery(id+"F0.wireOp",EDGE,"E3.0");Q5=makeQuery(id+"F9.boolean.opBoolean","SPLIT",EDGE,{"disambiguationData":[TD([makeQuery(id+"F1.opExtrude","SWEPT_FACE",FACE,{"disambiguationData":[OSD([subQ0])]})])],"derivedFrom":makeQuery(id+"F1.opExtrude","CAP_EDGE",EDGE,{"disambiguationData":[OSD([subQ2])],"isStart":false})});}
            var Q6;
            Q6=makeQuery(id+"F9.boolean.opBoolean","INTERSECT",EDGE,{"derivedFrom":[makeQuery(id+"F1.opExtrude","CAP_FACE",FACE,{"disambiguationData":[OSD([sQuery(id+"F0.wireOp",EDGE,"E0.bottom"),sQuery(id+"F0.wireOp",EDGE,"E1.2"),sQuery(id+"F0.wireOp",EDGE,"E2.0"),sQuery(id+"F0.wireOp",EDGE,"E3.0"),sQuery(id+"F0.wireOp",EDGE,"E8.bottom"),sQuery(id+"F0.wireOp",EDGE,"E8.left"),sQuery(id+"F0.wireOp",EDGE,"E8.right"),sQuery(id+"F0.wireOp",EDGE,"E9.filletArc"),sQuery(id+"F0.wireOp",EDGE,"E10.filletArc"),sQuery(id+"F0.wireOp",EDGE,"E11.filletArc"),sQuery(id+"F0.wireOp",EDGE,"E12"),sQuery(id+"F0.wireOp",EDGE,"E13.filletArc"),sQuery(id+"F0.wireOp",EDGE,"E14")])],"isStart":false}),makeQuery(id+"F9.opExtrude","SWEPT_FACE",FACE,{"disambiguationData":[OSD([sQuery(id+"F7.wireOp",EDGE,"E15.left")])]})]});
            var Q7;
            Q7=makeQuery(id+"F9.boolean.opBoolean","INTERSECT",EDGE,{"derivedFrom":[makeQuery(id+"F1.opExtrude","CAP_FACE",FACE,{"disambiguationData":[OSD([sQuery(id+"F0.wireOp",EDGE,"E0.bottom"),sQuery(id+"F0.wireOp",EDGE,"E1.2"),sQuery(id+"F0.wireOp",EDGE,"E2.0"),sQuery(id+"F0.wireOp",EDGE,"E3.0"),sQuery(id+"F0.wireOp",EDGE,"E8.bottom"),sQuery(id+"F0.wireOp",EDGE,"E8.left"),sQuery(id+"F0.wireOp",EDGE,"E8.right"),sQuery(id+"F0.wireOp",EDGE,"E9.filletArc"),sQuery(id+"F0.wireOp",EDGE,"E10.filletArc"),sQuery(id+"F0.wireOp",EDGE,"E11.filletArc"),sQuery(id+"F0.wireOp",EDGE,"E12"),sQuery(id+"F0.wireOp",EDGE,"E13.filletArc"),sQuery(id+"F0.wireOp",EDGE,"E14")])],"isStart":false}),makeQuery(id+"F9.opExtrude","SWEPT_FACE",FACE,{"disambiguationData":[OSD([sQuery(id+"F7.wireOp",EDGE,"E15.top")])]})]});
            var Q8;
            Q8=makeQuery(id+"F9.boolean.opBoolean","INTERSECT",EDGE,{"derivedFrom":[makeQuery(id+"F1.opExtrude","CAP_FACE",FACE,{"disambiguationData":[OSD([sQuery(id+"F0.wireOp",EDGE,"E0.bottom"),sQuery(id+"F0.wireOp",EDGE,"E1.2"),sQuery(id+"F0.wireOp",EDGE,"E2.0"),sQuery(id+"F0.wireOp",EDGE,"E3.0"),sQuery(id+"F0.wireOp",EDGE,"E8.bottom"),sQuery(id+"F0.wireOp",EDGE,"E8.left"),sQuery(id+"F0.wireOp",EDGE,"E8.right"),sQuery(id+"F0.wireOp",EDGE,"E9.filletArc"),sQuery(id+"F0.wireOp",EDGE,"E10.filletArc"),sQuery(id+"F0.wireOp",EDGE,"E11.filletArc"),sQuery(id+"F0.wireOp",EDGE,"E12"),sQuery(id+"F0.wireOp",EDGE,"E13.filletArc"),sQuery(id+"F0.wireOp",EDGE,"E14")])],"isStart":false}),makeQuery(id+"F9.opExtrude","SWEPT_FACE",FACE,{"disambiguationData":[OSD([sQuery(id+"F7.wireOp",EDGE,"E15.right")])]})]});
            var Q9;
            Q9=makeQuery(id+"F9.boolean.opBoolean","INTERSECT",EDGE,{"derivedFrom":[makeQuery(id+"F1.opExtrude","CAP_FACE",FACE,{"disambiguationData":[OSD([sQuery(id+"F0.wireOp",EDGE,"E0.bottom"),sQuery(id+"F0.wireOp",EDGE,"E1.2"),sQuery(id+"F0.wireOp",EDGE,"E2.0"),sQuery(id+"F0.wireOp",EDGE,"E3.0"),sQuery(id+"F0.wireOp",EDGE,"E8.bottom"),sQuery(id+"F0.wireOp",EDGE,"E8.left"),sQuery(id+"F0.wireOp",EDGE,"E8.right"),sQuery(id+"F0.wireOp",EDGE,"E9.filletArc"),sQuery(id+"F0.wireOp",EDGE,"E10.filletArc"),sQuery(id+"F0.wireOp",EDGE,"E11.filletArc"),sQuery(id+"F0.wireOp",EDGE,"E12"),sQuery(id+"F0.wireOp",EDGE,"E13.filletArc"),sQuery(id+"F0.wireOp",EDGE,"E14")])],"isStart":false}),makeQuery(id+"F9.opExtrude","SWEPT_FACE",FACE,{"disambiguationData":[OSD([sQuery(id+"F7.wireOp",EDGE,"E16")])]})]});
            var Q10;
            Q10=makeQuery(id+"F9.boolean.opBoolean","COPY",EDGE,{"derivedFrom":makeQuery(id+"F9.opExtrude","CAP_EDGE",EDGE,{"disambiguationData":[OSD([sQuery(id+"F7.wireOp",EDGE,"E16")])],"isStart":true})});
            var Q11;
            Q11=makeQuery(id+"F9.boolean.opBoolean","COPY",EDGE,{"derivedFrom":makeQuery(id+"F9.opExtrude","CAP_EDGE",EDGE,{"disambiguationData":[OSD([sQuery(id+"F7.wireOp",EDGE,"E15.top")])],"isStart":true})});
            var Q12;
            Q12=makeQuery(id+"F9.boolean.opBoolean","COPY",EDGE,{"derivedFrom":makeQuery(id+"F9.opExtrude","SWEPT_EDGE",EDGE,{"disambiguationData":[OSD([sQuery(id+"F7.wireOp",EDGE,"E15.top"),sQuery(id+"F7.wireOp",EDGE,"E15.right")])]})});
            var Q13;
            Q13=makeQuery(id+"F9.boolean.opBoolean","COPY",FACE,{"derivedFrom":makeQuery(id+"F9.opExtrude","SWEPT_FACE",FACE,{"disambiguationData":[OSD([sQuery(id+"F7.wireOp",EDGE,"E15.left")])]})});
            var Q14;
            Q14=makeQuery(id+"F1.opExtrude","CAP_FACE",FACE,{"disambiguationData":[OSD([sQuery(id+"F0.wireOp",EDGE,"E0.bottom"),sQuery(id+"F0.wireOp",EDGE,"E1.2"),sQuery(id+"F0.wireOp",EDGE,"E2.0"),sQuery(id+"F0.wireOp",EDGE,"E3.0"),sQuery(id+"F0.wireOp",EDGE,"E8.bottom"),sQuery(id+"F0.wireOp",EDGE,"E8.left"),sQuery(id+"F0.wireOp",EDGE,"E8.right"),sQuery(id+"F0.wireOp",EDGE,"E9.filletArc"),sQuery(id+"F0.wireOp",EDGE,"E10.filletArc"),sQuery(id+"F0.wireOp",EDGE,"E11.filletArc"),sQuery(id+"F0.wireOp",EDGE,"E12"),sQuery(id+"F0.wireOp",EDGE,"E13.filletArc"),sQuery(id+"F0.wireOp",EDGE,"E14")])],"isStart":false});
            var Q15;
            Q15=makeQuery(id+"F1.opExtrude","CAP_FACE",FACE,{"disambiguationData":[OSD([sQuery(id+"F0.wireOp",EDGE,"E0.bottom"),sQuery(id+"F0.wireOp",EDGE,"E1.2"),sQuery(id+"F0.wireOp",EDGE,"E2.0"),sQuery(id+"F0.wireOp",EDGE,"E3.0"),sQuery(id+"F0.wireOp",EDGE,"E8.bottom"),sQuery(id+"F0.wireOp",EDGE,"E8.left"),sQuery(id+"F0.wireOp",EDGE,"E8.right"),sQuery(id+"F0.wireOp",EDGE,"E9.filletArc"),sQuery(id+"F0.wireOp",EDGE,"E10.filletArc"),sQuery(id+"F0.wireOp",EDGE,"E11.filletArc"),sQuery(id+"F0.wireOp",EDGE,"E12"),sQuery(id+"F0.wireOp",EDGE,"E13.filletArc"),sQuery(id+"F0.wireOp",EDGE,"E14")])],"isStart":true});
            chamfer(context, id + "F11", {"entities" : qUnion([Q0, Q1, Q2, Q3, Q4, Q5, Q6, Q7, Q8, Q9, Q10, Q11, Q12, Q13, Q14, Q15]), "width" : 0.64 * mm, "tangentPropagation" : true});
        }
    });
